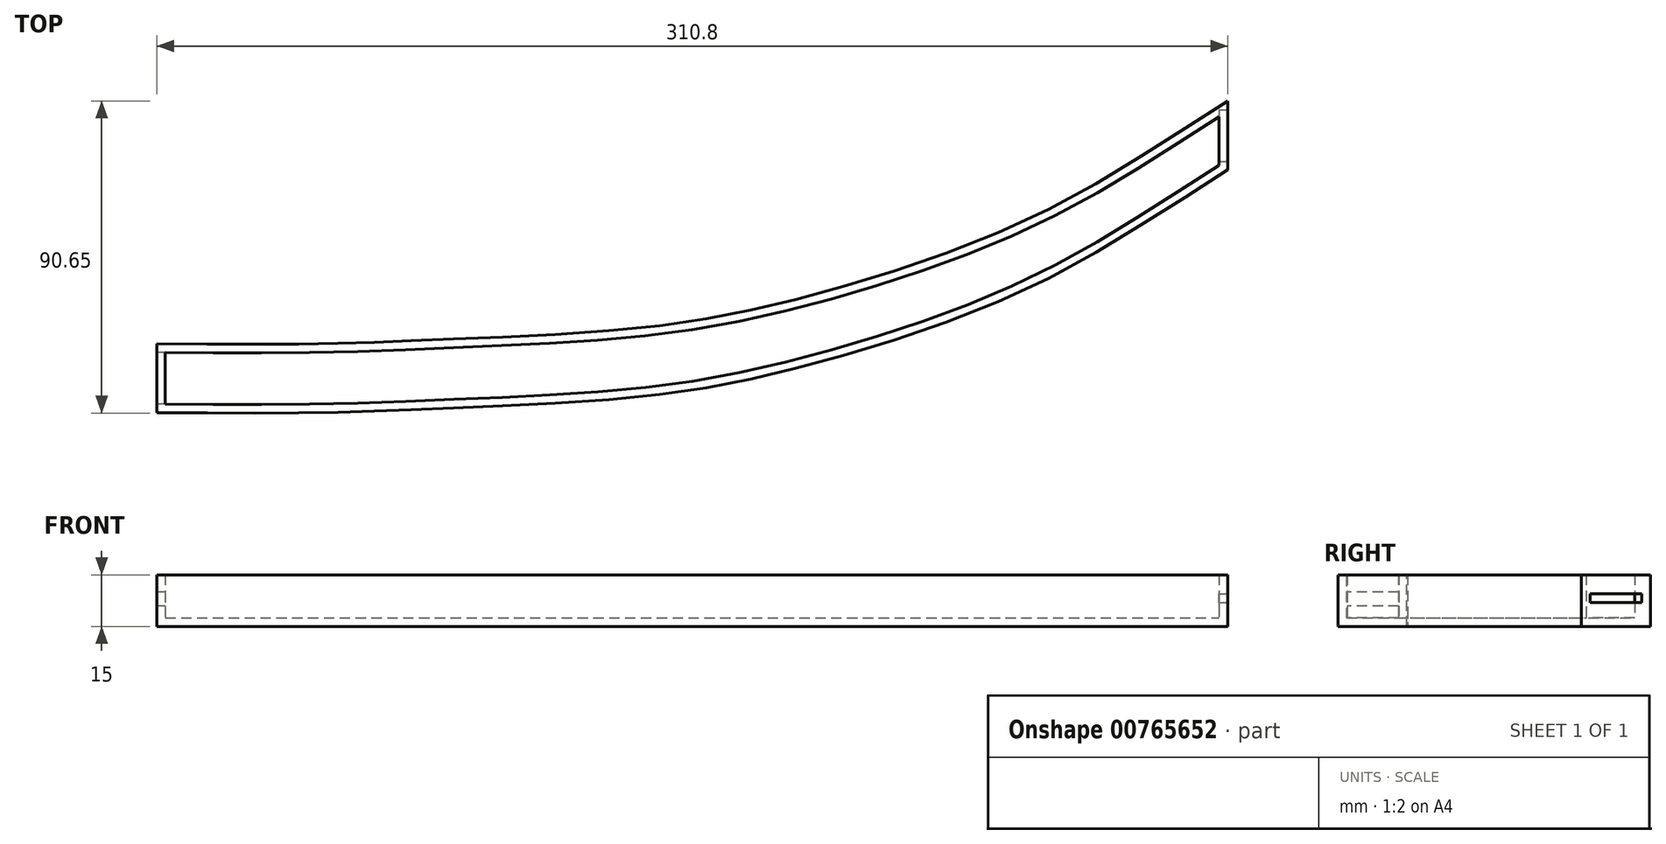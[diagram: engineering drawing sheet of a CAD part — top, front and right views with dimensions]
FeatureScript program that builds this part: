
annotation { "Feature Type Name" : "Feature", "Feature Type Description" : "" }
export const myFeature = defineFeature(function(context is Context, id is Id, definition is map)
    precondition{}
    {
        {
            var Q0;
            Q0=qCreatedBy(makeId("Top.planeOp"),FACE);
            var sketch = newSketch(context, id + "F0", { "sketchPlane" : qUnion([Q0])});
            skPoint(sketch, "E0.1.internal.orphan", {"position": v(49, 20) * mm});
            skPoint(sketch, "E0.2.internal.orphan", {"position": v(82, 21.2) * mm});
            skPoint(sketch, "E0.3.internal.orphan", {"position": v(192, 34.6) * mm});
            skPoint(sketch, "E0.4.internal.orphan", {"position": v(255.9, 57.6) * mm});
            skPoint(sketch, "E0.5.internal.orphan", {"position": v(310.8, 90.5) * mm});
            skPoint(sketch, "E0.start.orphan", {"position": v(0, 20) * mm});
            skFitSpline(sketch, "E1", {"points": [v(0, 20) * mm, v(49, 20) * mm, v(82, 21.2) * mm, v(142.6, 24.86) * mm, v(192, 34.6) * mm, v(255.9, 57.6) * mm, v(310.8, 90.5) * mm], "startDerivative": vector(347.02, -2.36) * mm, "endDerivative": vector(281.94, 176.78) * mm});
            skPoint(sketch, "E2.1.internal.orphan", {"position": v(49, 0) * mm});
            skPoint(sketch, "E2.2.internal.orphan", {"position": v(82, 1.2) * mm});
            skPoint(sketch, "E2.3.internal.orphan", {"position": v(192, 14.6) * mm});
            skPoint(sketch, "E2.4.internal.orphan", {"position": v(255.9, 37.6) * mm});
            skPoint(sketch, "E2.5.internal.orphan", {"position": v(310.8, 70.5) * mm});
            skPoint(sketch, "E2.start.orphan", {"position": v(0, 0) * mm});
            skFitSpline(sketch, "E3", {"points": [v(0, 0) * mm, v(49, 0) * mm, v(82, 1.2) * mm, v(142.6, 4.86) * mm, v(192, 14.6) * mm, v(255.9, 37.6) * mm, v(310.8, 70.5) * mm], "startDerivative": vector(347.02, -2.36) * mm, "endDerivative": vector(281.94, 176.78) * mm});
            skLineSegment(sketch, "E4", {"start": v(310.8, 90.5) * mm, "end": v(310.8, 70.5) * mm});
            skLineSegment(sketch, "E5", {"start": v(0, 20) * mm, "end": v(0, 0) * mm});
            skSolve(sketch);
        }
        {
            var Q0;
            Q0=makeQuery(id+"F0.imprint","IMPRINT",FACE,{"disambiguationData":[TD([[makeQuery(id+"F0.imprint","IMPRINT",EDGE,{"derivedFrom":sQuery(id+"F0.wireOp",EDGE,"E1")}),-1.0]])]});
            extrude(context, id + "F1", {"entities" : qUnion([Q0]), "depth" : 15 * mm, "offsetDistance" : 25 * mm});
        }
        {
            var Q0;
            Q0=makeQuery(id+"F1.opExtrude","CAP_FACE",FACE,{"disambiguationData":[OSD([sQuery(id+"F0.wireOp",EDGE,"E1"),sQuery(id+"F0.wireOp",EDGE,"E3"),sQuery(id+"F0.wireOp",EDGE,"E4"),sQuery(id+"F0.wireOp",EDGE,"E5")])],"isStart":false});
            shell(context, id + "F2", {"entities" : qUnion([Q0]), "thickness" : 2.5 * mm});
        }
        {
            var Q0;
            Q0=makeQuery(id+"F1.opExtrude","SWEPT_FACE",FACE,{"disambiguationData":[OSD([sQuery(id+"F0.wireOp",EDGE,"E5")])]});
            var sketch = newSketch(context, id + "F3", { "sketchPlane" : qUnion([Q0])});
            skLineSegment(sketch, "E6.bottom", {"start": v(-17.5, 10) * mm, "end": v(-2.5, 10) * mm});
            skLineSegment(sketch, "E6.top", {"start": v(-17.5, 6) * mm, "end": v(-2.5, 6) * mm});
            skLineSegment(sketch, "E6.left", {"start": v(-17.5, 10) * mm, "end": v(-17.5, 6) * mm});
            skLineSegment(sketch, "E6.right", {"start": v(-2.5, 10) * mm, "end": v(-2.5, 6) * mm});
            skSolve(sketch);
        }
        {
            var Q0;
            Q0 = qSketchRegion(id + "F3", true);
            var Q1;
            Q1=makeQuery(id+"F2.opShell","OFFSET_FACE",FACE,{"disambiguationData":[OSD([sQuery(id+"F0.wireOp",EDGE,"E5")])]});
            extrude(context, id + "F4", {"entities" : qUnion([Q0]), "operationType" : NewBodyOperationType.REMOVE, "endBound" : BoundingType.UP_TO_SURFACE, "oppositeDirection" : true, "depth" : 25 * mm, "endBoundEntityFace" : qUnion([Q1]), "offsetDistance" : 25 * mm});
        }
        {
            var Q0;
            Q0=makeQuery(id+"F1.opExtrude","SWEPT_FACE",FACE,{"disambiguationData":[OSD([sQuery(id+"F0.wireOp",EDGE,"E4")])]});
            var sketch = newSketch(context, id + "F5", { "sketchPlane" : qUnion([Q0])});
            skLineSegment(sketch, "E7.bottom", {"start": v(73, 9.5) * mm, "end": v(88, 9.5) * mm});
            skLineSegment(sketch, "E7.top", {"start": v(73, 7) * mm, "end": v(88, 7) * mm});
            skLineSegment(sketch, "E7.left", {"start": v(73, 9.5) * mm, "end": v(73, 7) * mm});
            skLineSegment(sketch, "E7.right", {"start": v(88, 9.5) * mm, "end": v(88, 7) * mm});
            skSolve(sketch);
        }
        {
            var Q0;
            Q0 = qSketchRegion(id + "F5", true);
            var Q1;
            Q1=makeQuery(id+"F2.opShell","OFFSET_FACE",FACE,{"disambiguationData":[OSD([sQuery(id+"F0.wireOp",EDGE,"E4")])]});
            extrude(context, id + "F6", {"entities" : qUnion([Q0]), "operationType" : NewBodyOperationType.REMOVE, "endBound" : BoundingType.UP_TO_SURFACE, "oppositeDirection" : true, "depth" : 25 * mm, "endBoundEntityFace" : qUnion([Q1]), "offsetDistance" : 25 * mm});
        }
    });
